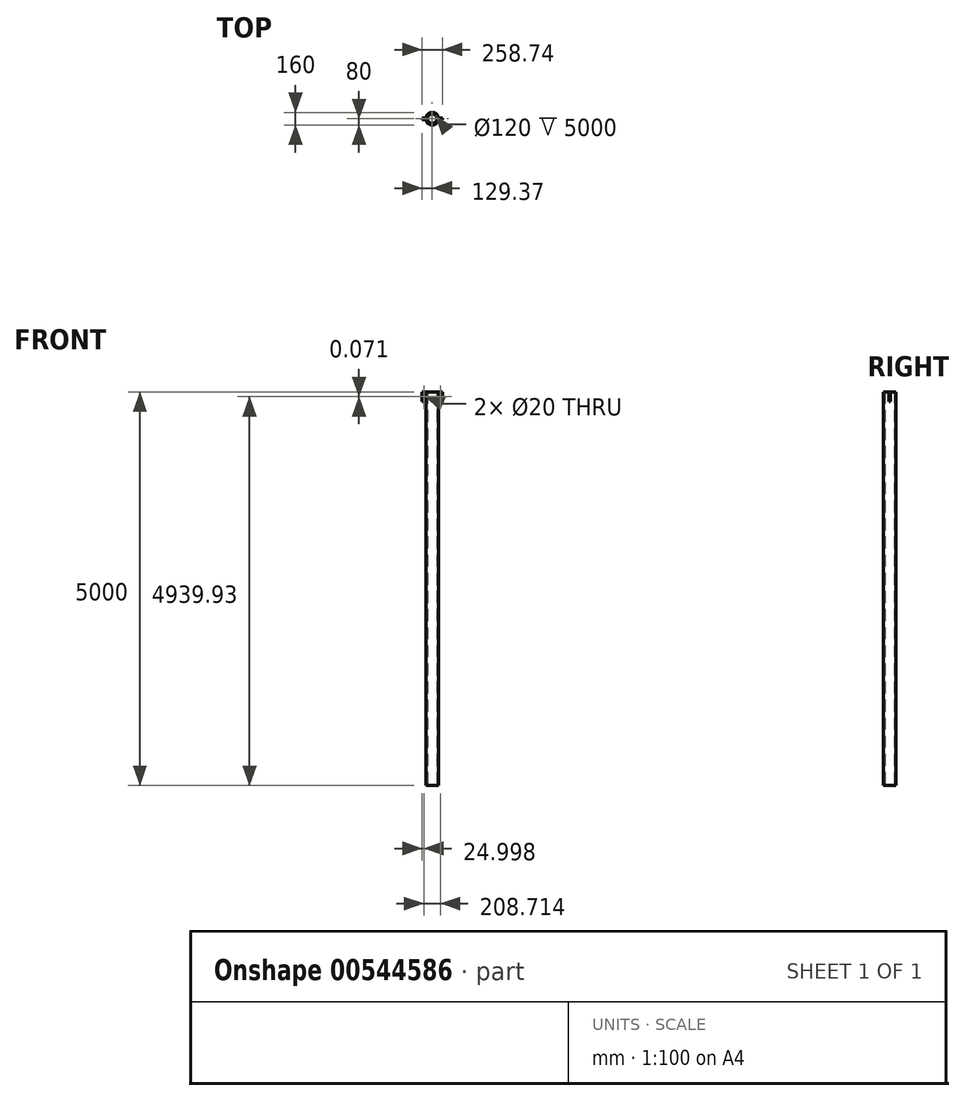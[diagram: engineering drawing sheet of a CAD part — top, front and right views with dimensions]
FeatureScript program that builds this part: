
annotation { "Feature Type Name" : "Feature", "Feature Type Description" : "" }
export const myFeature = defineFeature(function(context is Context, id is Id, definition is map)
    precondition{}
    {
        {
            var Q0;
            Q0=qCreatedBy(makeId("Front.planeOp"),FACE);
            var sketch = newSketch(context, id + "F0", { "sketchPlane" : qUnion([Q0])});
            skLineSegment(sketch, "E0.left", {"start": v(0, 0) * mm, "end": v(0, 5000) * mm});
            skLineSegment(sketch, "E0.right", {"start": v(60, 0) * mm, "end": v(60, 5000) * mm});
            skLineSegment(sketch, "E1.right", {"start": v(80, 0) * mm, "end": v(80, 5000) * mm});
            skLineSegment(sketch, "E2", {"start": v(60, 0) * mm, "end": v(80, 0) * mm});
            skLineSegment(sketch, "E3", {"start": v(60, 5000) * mm, "end": v(80, 5000) * mm});
            skSolve(sketch);
        }
        {
            var Q0;
            Q0=makeQuery(id+"F0.imprint","IMPRINT",FACE,{"disambiguationData":[TD([[makeQuery(id+"F0.imprint","IMPRINT",EDGE,{"derivedFrom":sQuery(id+"F0.wireOp",EDGE,"E0.right")}),-1.0]])]});
            var Q1;
            Q1=sQuery(id+"F0.wireOp",EDGE,"E0.left");
            revolve(context, id + "F1", {"entities" : qUnion([Q0]), "axis" : qUnion([Q1]), "revolveType" : RevolveType.FULL});
        }
        {
            var Q0;
            Q0=makeQuery(id+"F1.opRevolve","SWEPT_FACE",FACE,{"disambiguationData":[OSD([sQuery(id+"F0.wireOp",EDGE,"E3")])]});
            var sketch = newSketch(context, id + "F2", { "sketchPlane" : qUnion([Q0])});
            skLineSegment(sketch, "E4.bottom", {"start": v(-79.37, 10) * mm, "end": v(-129.37, 10) * mm});
            skLineSegment(sketch, "E4.top", {"start": v(-79.37, -10) * mm, "end": v(-129.37, -10) * mm});
            skLineSegment(sketch, "E4.right", {"start": v(-129.37, 10) * mm, "end": v(-129.37, -10) * mm});
            skLineSegment(sketch, "E5.bottom", {"start": v(79.37, -10) * mm, "end": v(129.37, -10) * mm});
            skLineSegment(sketch, "E5.top", {"start": v(79.37, 10) * mm, "end": v(129.37, 10) * mm});
            skLineSegment(sketch, "E5.right", {"start": v(129.37, -10) * mm, "end": v(129.37, 10) * mm});
            skArc(sketch, "E6", {"start": v(-79.37, 10) * mm, "mid": v(-80, 0) * mm, "end": v(-79.37, -10) * mm});
            skArc(sketch, "E7.trimOffspring", {"start": v(79.37, -10) * mm, "mid": v(80, 0) * mm, "end": v(79.37, 10) * mm});
            skSolve(sketch);
        }
        {
            var Q0;
            Q0=makeQuery(id+"F2.imprint","IMPRINT",FACE,{"disambiguationData":[TD([[makeQuery(id+"F2.imprint","IMPRINT",EDGE,{"derivedFrom":sQuery(id+"F2.wireOp",EDGE,"E4.bottom")}),1.0]])]});
            var Q1;
            Q1=makeQuery(id+"F2.imprint","IMPRINT",FACE,{"disambiguationData":[TD([[makeQuery(id+"F2.imprint","IMPRINT",EDGE,{"derivedFrom":sQuery(id+"F2.wireOp",EDGE,"E5.bottom")}),1.0]])]});
            extrude(context, id + "F3", {"entities" : qUnion([Q0, Q1]), "operationType" : NewBodyOperationType.ADD, "oppositeDirection" : true, "depth" : 120 * mm, "offsetDistance" : 25 * mm});
        }
        {
            var Q0;
            Q0=makeQuery(id+"F3.opExtrude","SWEPT_FACE",FACE,{"disambiguationData":[OSD([sQuery(id+"F2.wireOp",EDGE,"E4.top")])]});
            var sketch = newSketch(context, id + "F4", { "sketchPlane" : qUnion([Q0])});
            skCircle(sketch, "E8", {"center": v(-104.37, 4940) * mm, "radius": 10 * mm});
            skCircle(sketch, "E9", {"center": v(104.34, 4939.93) * mm, "radius": 10 * mm});
            skSolve(sketch);
        }
        {
            var Q0;
            Q0 = qSketchRegion(id + "F4", true);
            extrude(context, id + "F5", {"entities" : qUnion([Q0]), "operationType" : NewBodyOperationType.REMOVE, "oppositeDirection" : true, "depth" : 25 * mm, "offsetDistance" : 25 * mm});
        }
    });
